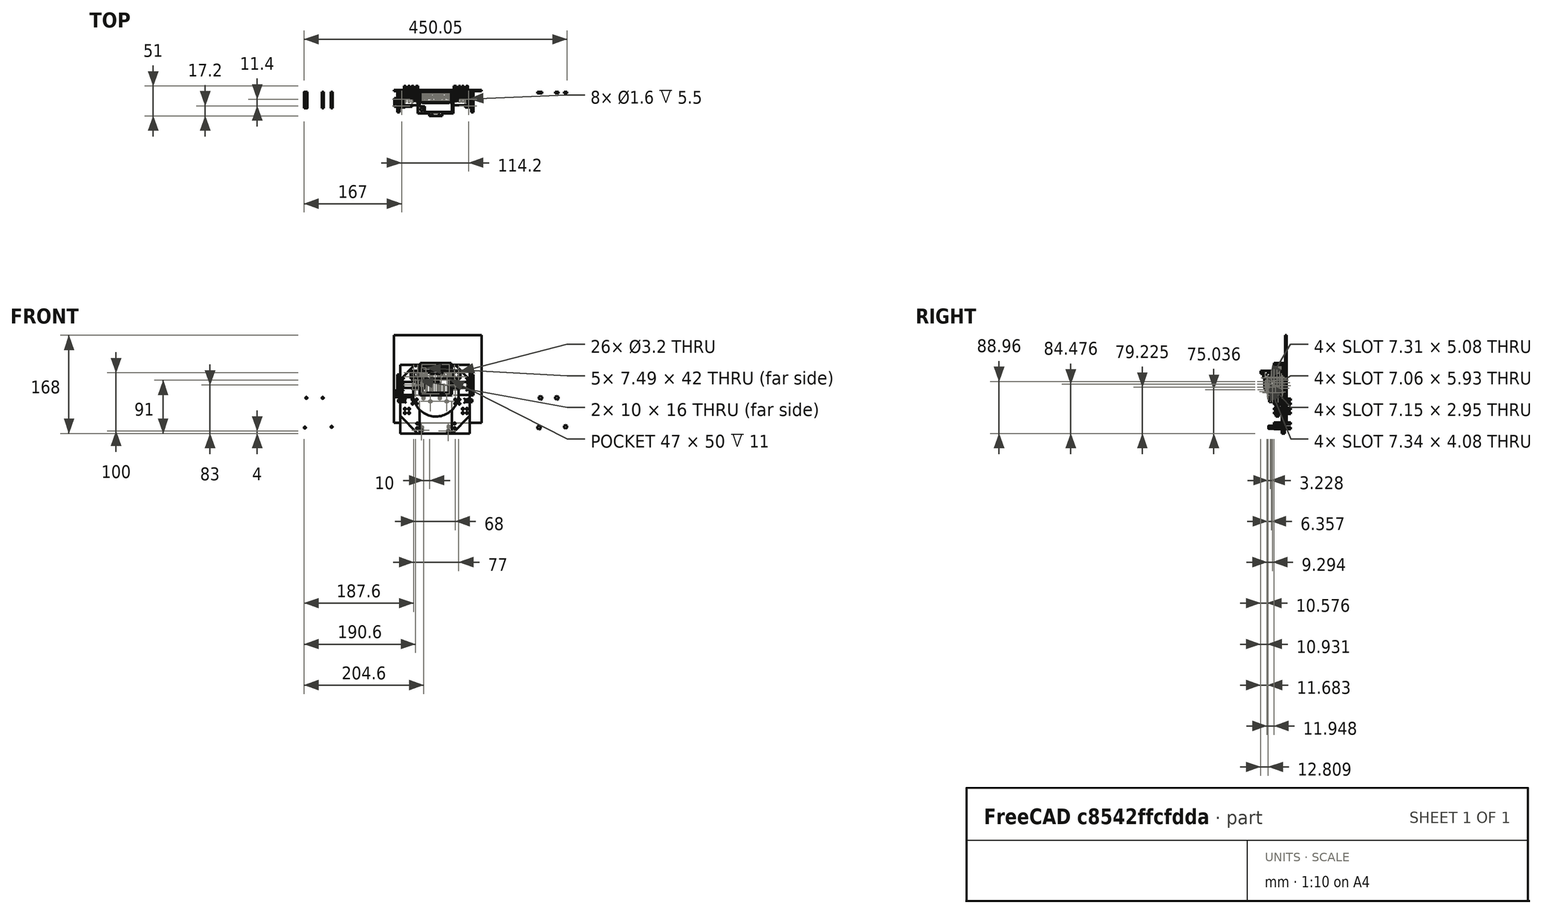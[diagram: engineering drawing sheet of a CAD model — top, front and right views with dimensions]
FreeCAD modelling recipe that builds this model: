
FCSTD DOCUMENT  (FreeCAD 0.16R6712 (Git))
Label: 5028.2 Frank the Robot
License: All rights reserved
LicenseURL: http://en.wikipedia.org/wiki/All_rights_reserved
objects: Part::Cylinder×87, Part::Cut×49, Part::Fuse×46, Part::Box×45, Part::MultiFuse×20, Part::Feature×17, Part::Fillet×10, Part::Mirroring×8, Part::Chamfer×7, Part::Cone×4, Part::Compound×3, Part::Torus×2, App::DocumentObjectGroup×1
note: 298 computed .brp shape members not serialized (recipe doc carries the construction recipe); baked Part::Feature solids carry a one-line shape summary decoded from their .brp

FEATURE [Part::Cylinder] Cylinder
  Angle = 360
  Height = 30
  Radius = 7
FEATURE [Part::Cylinder] Cylinder001
  Angle = 360
  Height = 19
  Placement = pos=(0,0,30) rot=(0,0,1;0rad)
  Radius = 7
FEATURE [Part::Cylinder] Cylinder002
  Angle = 360
  Height = 1.8
  Placement = pos=(0,0,49) rot=(0,0,1;0rad)
  Radius = 2.5
FEATURE [Part::Compound] Compound
  Links = -> [Cylinder,Cylinder002,Cylinder001]
FEATURE [Part::Cylinder] Cylinder003
  Angle = 360
  Height = 30
  Radius = 7
FEATURE [Part::Cylinder] Cylinder004
  Angle = 360
  Height = 19
  Placement = pos=(0,0,30) rot=(0,0,1;0rad)
  Radius = 7
FEATURE [Part::Cylinder] Cylinder005
  Angle = 360
  Height = 1.8
  Placement = pos=(0,0,49) rot=(0,0,1;0rad)
  Radius = 2.5
FEATURE [Part::Compound] Compound001
  Links = -> [Cylinder003,Cylinder005,Cylinder004]
  Placement = pos=(14.5,0,50) rot=(1,0,0;3.14159rad)
FEATURE [Part::Cylinder] Cylinder006
  Angle = 360
  Height = 30
  Radius = 7
FEATURE [Part::Cylinder] Cylinder007
  Angle = 360
  Height = 19
  Placement = pos=(0,0,30) rot=(0,0,1;0rad)
  Radius = 7
FEATURE [Part::Cylinder] Cylinder008
  Angle = 360
  Height = 1.8
  Placement = pos=(0,0,49) rot=(0,0,1;0rad)
  Radius = 2.5
FEATURE [Part::Compound] Compound002
  Links = -> [Cylinder006,Cylinder008,Cylinder007]
  Placement = pos=(29,0,0) rot=(0,0,1;0rad)
FEATURE [Part::Box] Box  label="Cube"
  Height = 50
  Length = 47
  Placement = pos=(-9,-8,0) rot=(0,0,1;0rad)
  Width = 12
FEATURE [Part::Box] Box001  label="Cube001"
  Height = 55
  Length = 53
  Placement = pos=(-12,-8,-2.5) rot=(0,0,1;0rad)
  Width = 11
FEATURE [Part::Cylinder] Cylinder009
  Angle = 360
  Height = 50
  Radius = 7
FEATURE [Part::Cylinder] Cylinder010
  Angle = 360
  Height = 50
  Placement = pos=(14.5,0,0) rot=(0,0,1;0rad)
  Radius = 7
FEATURE [Part::Cut] Cut
  Base = -> Box001
  Tool = -> Box
FEATURE [Part::Box] Box002  label="Cube002"
  Height = 55
  Length = 53
  Placement = pos=(-12,3,-2.5) rot=(0,0,1;0rad)
  Width = 7
FEATURE [Part::Fuse] Fusion
  Base = -> Cut
  Tool = -> Box002
FEATURE [Part::Cut] Cut001  label="No idea why this is here...."
  Base = -> Fusion
  Tool = -> Cylinder009
FEATURE [Part::Cylinder] Cylinder011
  Angle = 360
  Height = 50
  Placement = pos=(29,0,0) rot=(0,0,1;0rad)
  Radius = 7
FEATURE [Part::Box] Box003  label="Cube003"
  Height = 5
  Length = 2
  Placement = pos=(28,-9,-2) rot=(0,0,1;0rad)
  Width = 12
FEATURE [Part::Box] Box004  label="Cube004"
  Height = 5
  Length = 2
  Placement = pos=(18.5,-9,46) rot=(0,0,1;0rad)
  Width = 12
FEATURE [Part::Box] Box005  label="Cube005"
  Height = 5
  Length = 2
  Placement = pos=(-2,-9,46) rot=(0,0,1;0rad)
  Width = 12
FEATURE [Part::Box] Box006  label="Cube006"
  Height = 5
  Length = 3
  Placement = pos=(35,-9,-4) rot=(0,0,1;0rad)
  Width = 12
FEATURE [Part::Cut] Cut008
FEATURE [Part::Torus] Torus001
  Angle1 = -180
  Angle2 = 180
  Angle3 = 360
  Placement = pos=(0,0,2) rot=(0,0,1;0rad)
  Radius1 = 19
  Radius2 = 1.5
FEATURE [Part::Cut] Cut009  label="wheel2"
  Base = -> Cut008
  Placement = pos=(75,-7,15) rot=(0,1,0;1.5708rad)
  Tool = -> Torus001
FEATURE [Part::Torus] Torus
  Angle1 = -180
  Angle2 = 180
  Angle3 = 360
  Placement = pos=(0,0,2) rot=(0,0,1;0rad)
  Radius1 = 19
  Radius2 = 1.5
FEATURE [Part::Cut] Cut010
FEATURE [Part::Cut] Cut011  label="wheel1"
  Base = -> Cut010
  Placement = pos=(-51,-7,15) rot=(0,1,0;1.5708rad)
  Tool = -> Torus
FEATURE [Part::Fuse] Fusion003
FEATURE [Part::Cylinder] Cylinder012
  Angle = 360
  Height = 10
  Placement = pos=(5,-4.5,0) rot=(0,1,0;1.5708rad)
  Radius = 0.8
FEATURE [Part::Fuse] Fusion048  label="right-motor001"
  Base = -> Cylinder012
  Placement = pos=(-51,-7,15) rot=(0,0,1;0rad)
  Tool = -> Fusion003
FEATURE [Part::Fuse] Fusion049
FEATURE [Part::Cylinder] Cylinder013
  Angle = 360
  Height = 10
  Placement = pos=(5,-4.5,0) rot=(0,1,0;1.5708rad)
  Radius = 0.8
FEATURE [Part::Fuse] Fusion050  label="left-motor001"
  Base = -> Cylinder013
  Placement = pos=(79,-7,15) rot=(0,0,1;3.14159rad)
  Tool = -> Fusion049
FEATURE [Part::Box] Box007  label="Cube007"
  Height = 5
  Length = 2
  Placement = pos=(37.5,-9,46) rot=(0,0,1;0rad)
  Width = 12
FEATURE [Part::Box] Box008  label="Cube008"
  Height = 5
  Length = 2
  Placement = pos=(8,-9,-2) rot=(0,0,1;0rad)
  Width = 12
FEATURE [Part::Box] Box009  label="The Ground"
  Height = 150
  Length = 150
  Placement = pos=(-57,11,-50) rot=(0,0,1;0rad)
  Width = 2
FEATURE [Part::Box] Box010  label="Motor Mount Left"
  Height = 16
  Length = 4
  Placement = pos=(69,-13,7) rot=(0,0,1;0rad)
  Width = 20
FEATURE [Part::Box] Box011  label="Motor Mount Right"
  Height = 16
  Length = 4
  Placement = pos=(-46,-13,7) rot=(0,0,1;0rad)
  Width = 20
FEATURE [Part::Box] Box012  label="Motor Support Right"
  Height = 16
  Length = 10
  Placement = pos=(-25,-1,7) rot=(0,0,1;0rad)
  Width = 8
FEATURE [Part::Box] Box013  label="Motor Support Left"
  Height = 16
  Length = 10
  Placement = pos=(43,-1,7) rot=(0,0,1;0rad)
  Width = 8
FEATURE [Part::Cylinder] Cylinder014
  Angle = 360
  Height = 28
  Placement = pos=(40.7,0,-10.3) rot=(1,0,0;1.5708rad)
  Radius = 1.6
FEATURE [Part::Cylinder] Cylinder015
  Angle = 360
  Height = 28
  Placement = pos=(-2.4,0,-59.8) rot=(1,0,0;1.5708rad)
  Radius = 1.6
FEATURE [Part::Cylinder] Cylinder016
  Angle = 360
  Height = 28
  Placement = pos=(-5,0,-9) rot=(1,0,0;1.5708rad)
  Radius = 1.6
FEATURE [Part::Cylinder] Cylinder017
  Angle = 360
  Height = 28
  Placement = pos=(25.5,0,-59.8) rot=(1,0,0;1.5708rad)
  Radius = 1.6
FEATURE [Part::Fuse] Fusion051
  Base = -> Cylinder015
  Tool = -> Cylinder016
FEATURE [Part::Fuse] Fusion052
  Base = -> Cylinder014
  Tool = -> Cylinder017
FEATURE [Part::Fuse] Fusion053  label="Screw holes on Arduino Duo"
  Base = -> Fusion051
  Tool = -> Fusion052
FEATURE [Part::Mirroring] Part__Mirroring  label="XXXXXScrew holes on Arduino Duo (Mirror #1)"
  Base = (0,0,0)
  Normal = (0,0,1)
  Placement = pos=(-204,10,-67) rot=(0,0,1;0rad)
  Source = -> Fusion053
FEATURE [Part::Box] Box014  label="Not used Cube"
  Height = 51
  Length = 119
  Placement = pos=(-46,7,-2) rot=(0,0,1;0rad)
  Width = 3
FEATURE [Part::Box] Box015  label="Cube014 Arduino Support cube"
  Height = 67
  Length = 55
  Placement = pos=(-13,5,-68) rot=(0,0,1;0rad)
  Width = 5
FEATURE [Part::Cylinder] Cylinder018
  Angle = 360
  Height = 5
  Placement = pos=(15,0,0) rot=(1,0,0;1.5708rad)
  Radius = 39
FEATURE [Part::Cut] Cut014  label="M3 Nut"
  Base = -> Cut001
  Placement = pos=(-6.4,10,-7.2) rot=(1,0,0;1.5708rad)
  Tool = -> Cylinder001
FEATURE [Part::Cut] Cut015  label="M3 Nut001"
  Base = -> Cut001
  Placement = pos=(21.5,10,-7.2) rot=(1,0,0;1.5708rad)
  Tool = -> Cylinder001
FEATURE [Part::Cut] Cut016  label="M3 Nut002"
  Base = -> Cut001
  Placement = pos=(36.7,10,-56.7) rot=(1,0,0;1.5708rad)
  Tool = -> Cylinder001
FEATURE [Part::Cut] Cut017  label="M3 Nut003"
  Base = -> Cut001
  Placement = pos=(-9,10,-58) rot=(1,0,0;1.5708rad)
  Tool = -> Cylinder001
FEATURE [Part::Cut] Cut018
  Base = -> Cut
  Placement = pos=(-9,10,-58) rot=(1,0,0;1.5708rad)
  Tool = -> Box006
FEATURE [Part::Cut] Cut019
  Base = -> Cut
  Placement = pos=(36.7,10,-56.7) rot=(1,0,0;1.5708rad)
  Tool = -> Box006
FEATURE [Part::Cut] Cut020
  Base = -> Cut
  Placement = pos=(-6.4,10,-7.2) rot=(1,0,0;1.5708rad)
  Tool = -> Box006
FEATURE [Part::Cut] Cut021
  Base = -> Cut
  Placement = pos=(21.5,10,-7.2) rot=(1,0,0;1.5708rad)
  Tool = -> Box006
FEATURE [Part::MultiFuse] Fusion054  label="XXXXXHex Holes"
  Placement = pos=(200,0,0) rot=(0,0,1;0rad)
  Shapes = -> [Cut018,Cut021,Cut019,Cut020]
FEATURE [Part::Box] Box016  label="Cube015"
  Height = 117
  Length = 33
  Placement = pos=(-46,7,-68) rot=(0,0,1;0rad)
  Width = 3
FEATURE [Part::Box] Box017  label="Cube016"
  Height = 117
  Length = 31
  Placement = pos=(42,7,-68) rot=(0,0,1;0rad)
  Width = 3
FEATURE [Part::Cylinder] Cylinder019
  Angle = 360
  Height = 28
  Placement = pos=(48,20,-10) rot=(1,0,0;1.5708rad)
  Radius = 1.6
FEATURE [Part::Cylinder] Cylinder020
  Angle = 360
  Height = 28
  Placement = pos=(47,20,-51) rot=(1,0,0;1.5708rad)
  Radius = 1.6
FEATURE [Part::Cylinder] Cylinder021
  Angle = 360
  Height = 28
  Placement = pos=(48,20,-17) rot=(1,0,0;1.5708rad)
  Radius = 1.6
FEATURE [Part::Cylinder] Cylinder022
  Angle = 360
  Height = 28
  Placement = pos=(47,20,-59) rot=(1,0,0;1.5708rad)
  Radius = 1.6
FEATURE [Part::Cylinder] Cylinder023
  Angle = 360
  Height = 28
  Placement = pos=(55,20,-17) rot=(1,0,0;1.5708rad)
  Radius = 1.6
FEATURE [Part::Cylinder] Cylinder024
  Angle = 360
  Height = 28
  Placement = pos=(55,20,-10) rot=(1,0,0;1.5708rad)
  Radius = 1.6
FEATURE [Part::MultiFuse] Fusion055
  Shapes = -> [Cylinder021,Cylinder023,Cylinder024,Cylinder019]
FEATURE [Part::MultiFuse] Fusion056
  Placement = pos=(13,0,-16) rot=(0,0,1;0rad)
  Shapes = -> [Cylinder021,Cylinder023,Cylinder024,Cylinder019]
FEATURE [Part::MultiFuse] Fusion057  label="Mount holes top left"
  Placement = pos=(-1,0,46) rot=(0,0,1;0rad)
  Shapes = -> [Cylinder021,Cylinder023,Cylinder024,Cylinder019]
FEATURE [Part::MultiFuse] Fusion058  label="Mount holes top right"
  Placement = pos=(-71,0,46) rot=(0,0,1;0rad)
  Shapes = -> [Cylinder021,Cylinder023,Cylinder024,Cylinder019]
FEATURE [Part::MultiFuse] Fusion059
  Shapes = -> [Cylinder022,Cylinder020,Fusion055,Fusion056]
FEATURE [Part::Mirroring] Part__Mirroring001  label="Mount holes bottom right"
  Base = (0,0,0)
  Normal = (1,0,0)
  Placement = pos=(30,0,0) rot=(0,0,1;0rad)
  Source = -> Fusion059
FEATURE [Part::Cylinder] Cylinder025
  Angle = 360
  Height = 28
  Placement = pos=(48,20,-10) rot=(1,0,0;1.5708rad)
  Radius = 1.6
FEATURE [Part::Cylinder] Cylinder026
  Angle = 360
  Height = 28
  Placement = pos=(47,20,-51) rot=(1,0,0;1.5708rad)
  Radius = 1.6
FEATURE [Part::Cylinder] Cylinder027
  Angle = 360
  Height = 28
  Placement = pos=(48,20,-17) rot=(1,0,0;1.5708rad)
  Radius = 1.6
FEATURE [Part::Cylinder] Cylinder028
  Angle = 360
  Height = 28
  Placement = pos=(47,20,-59) rot=(1,0,0;1.5708rad)
  Radius = 1.6
FEATURE [Part::Cylinder] Cylinder029
  Angle = 360
  Height = 28
  Placement = pos=(55,20,-17) rot=(1,0,0;1.5708rad)
  Radius = 1.6
FEATURE [Part::Cylinder] Cylinder030
  Angle = 360
  Height = 28
  Placement = pos=(55,20,-10) rot=(1,0,0;1.5708rad)
  Radius = 1.6
FEATURE [Part::MultiFuse] Fusion060
  Shapes = -> [Cylinder027,Cylinder029,Cylinder030,Cylinder025]
FEATURE [Part::MultiFuse] Fusion061
  Placement = pos=(13,0,-16) rot=(0,0,1;0rad)
  Shapes = -> [Cylinder027,Cylinder029,Cylinder030,Cylinder025]
FEATURE [Part::MultiFuse] Fusion062  label="Mount holes bottom left"
  Shapes = -> [Cylinder028,Cylinder026,Fusion060,Fusion061]
FEATURE [Part::Cylinder] Cylinder031  label="Cylinder083"
  Angle = 360
  Height = 10
  Placement = pos=(0,18,29) rot=(0,0,1;0rad)
  Radius = 2.25
FEATURE [Part::Cylinder] Cylinder032  label="Cylinder084"
  Angle = 360
  Height = 10
  Placement = pos=(4.5,18,32) rot=(0,0,1;0rad)
  Radius = 1
FEATURE [Part::Cylinder] Cylinder033  label="Cylinder085"
  Angle = 360
  Height = 10
  Placement = pos=(-4.5,18,32) rot=(0,0,1;0rad)
  Radius = 1
FEATURE [Part::Fuse] Fusion009  label="Mounting Screw Holes"
  Base = -> Cylinder032
  Tool = -> Cylinder033
FEATURE [Part::Fuse] Fusion071  label="Motor Holes Left"
  Base = -> Cylinder031
  Placement = pos=(37,-7,-3) rot=(0.57735,0.57735,0.57735;2.0944rad)
  Tool = -> Fusion009
FEATURE [Part::Cylinder] Cylinder034  label="Cylinder086"
  Angle = 360
  Height = 10
  Placement = pos=(0,18,29) rot=(0,0,1;0rad)
  Radius = 2.25
FEATURE [Part::Cylinder] Cylinder035  label="Cylinder087"
  Angle = 360
  Height = 10
  Placement = pos=(4.5,18,32) rot=(0,0,1;0rad)
  Radius = 1
FEATURE [Part::Cylinder] Cylinder036  label="Cylinder088"
  Angle = 360
  Height = 10
  Placement = pos=(-4.5,18,32) rot=(0,0,1;0rad)
  Radius = 1
FEATURE [Part::Fuse] Fusion072  label="Mounting Screw Holes001"
  Base = -> Cylinder035
  Tool = -> Cylinder036
FEATURE [Part::Fuse] Fusion073  label="Motor Holes Right"
  Base = -> Cylinder034
  Placement = pos=(-79,-7,-3) rot=(0.57735,0.57735,0.57735;2.0944rad)
  Tool = -> Fusion072
FEATURE [Part::Cylinder] Cylinder037  label="Cylinder089"
  Angle = 360
  Height = 28
  Placement = pos=(40.7,0,-10.3) rot=(1,0,0;1.5708rad)
  Radius = 1.6
FEATURE [Part::Cylinder] Cylinder038  label="Cylinder090"
  Angle = 360
  Height = 28
  Placement = pos=(-2.4,0,-59.8) rot=(1,0,0;1.5708rad)
  Radius = 1.6
FEATURE [Part::Cylinder] Cylinder039  label="Cylinder091"
  Angle = 360
  Height = 28
  Placement = pos=(-5,0,-9) rot=(1,0,0;1.5708rad)
  Radius = 1.6
FEATURE [Part::Cylinder] Cylinder040  label="Cylinder092"
  Angle = 360
  Height = 28
  Placement = pos=(25.5,0,-59.8) rot=(1,0,0;1.5708rad)
  Radius = 1.6
FEATURE [Part::Fuse] Fusion074
  Base = -> Cylinder038
  Tool = -> Cylinder039
FEATURE [Part::Fuse] Fusion075
  Base = -> Cylinder037
  Tool = -> Cylinder040
FEATURE [Part::Fuse] Fusion076  label="Screw holes on Arduino Duo001"
  Base = -> Fusion074
  Tool = -> Fusion075
FEATURE [Part::Mirroring] Part__Mirroring002  label="Screw holes on Arduino Duo (Mirror #1)001"
  Base = (0,0,0)
  Normal = (0,0,1)
  Placement = pos=(-4,10,-67) rot=(0,0,1;0rad)
  Source = -> Fusion076
FEATURE [Part::Mirroring] Part__Mirroring003  label="Screw holes on Arduino Duo (Mirror #1)001 (Mirror #4)"
  Base = (0,0,0)
  Normal = (1,0,0)
  Placement = pos=(27,0,-6) rot=(0,0,1;0rad)
  Source = -> Part__Mirroring002
FEATURE [Part::Box] Box018  label="Cube017"
  Height = 50
  Length = 47
  Placement = pos=(-9,-8,0) rot=(0,0,1;0rad)
  Width = 12
FEATURE [Part::Box] Box019  label="Cube018"
  Height = 55
  Length = 53
  Placement = pos=(-12,-8,-2.5) rot=(0,0,1;0rad)
  Width = 11
FEATURE [Part::Cut] Cut031
  Base = -> Box019
  Tool = -> Box018
FEATURE [Part::Box] Box020  label="Cube019"
  Height = 5
  Length = 3
  Placement = pos=(35,-9,-4) rot=(0,0,1;0rad)
  Width = 12
FEATURE [Part::Cut] Cut032
  Base = -> Cut031
  Placement = pos=(-9,10,-58) rot=(1,0,0;1.5708rad)
  Tool = -> Box020
FEATURE [Part::Cut] Cut033
  Base = -> Cut031
  Placement = pos=(36.7,10,-56.7) rot=(1,0,0;1.5708rad)
  Tool = -> Box020
FEATURE [Part::Cut] Cut034
  Base = -> Cut031
  Placement = pos=(-6.4,10,-7.2) rot=(1,0,0;1.5708rad)
  Tool = -> Box020
FEATURE [Part::Cut] Cut035
  Base = -> Cut031
  Placement = pos=(21.5,10,-7.2) rot=(1,0,0;1.5708rad)
  Tool = -> Box020
FEATURE [Part::MultiFuse] Fusion077
  Shapes = -> [Cut032,Cut035,Cut033,Cut034]
FEATURE [Part::Mirroring] Part__Mirroring004  label="Hex Holes"
  Base = (0,0,0)
  Normal = (1,0,0)
  Placement = pos=(27,0,-6) rot=(0,0,1;0rad)
  Source = -> Fusion077
FEATURE [Part::Box] Box021  label="Cube020"
  Height = 13
  Length = 61
  Placement = pos=(-16,-27,26) rot=(0,0,1;0rad)
  Width = 34
FEATURE [Part::Box] Box022  label="Cube021"
  Height = 13
  Length = 12
  Placement = pos=(45,4,26) rot=(0,0,1;0rad)
  Width = 3
FEATURE [Part::Box] Box023  label="Cube022"
  Height = 13
  Length = 12
  Placement = pos=(-28,4,26) rot=(0,0,1;0rad)
  Width = 3
FEATURE [Part::Box] Box024  label="Cube023"
  Height = 13
  Length = 55
  Placement = pos=(-13,-24,26) rot=(0,0,1;0rad)
  Width = 31
FEATURE [Part::Cylinder] Cylinder041  label="Cylinder093"
  Angle = 360
  Height = 28
  Placement = pos=(54,20,29) rot=(1,0,0;1.5708rad)
  Radius = 1.6
FEATURE [Part::Cylinder] Cylinder042  label="Cylinder094"
  Angle = 360
  Height = 28
  Placement = pos=(54,20,36) rot=(1,0,0;1.5708rad)
  Radius = 1.6
FEATURE [Part::Cylinder] Cylinder043  label="Cylinder095"
  Angle = 360
  Height = 28
  Placement = pos=(-23,20,29) rot=(1,0,0;1.5708rad)
  Radius = 1.6
FEATURE [Part::Cylinder] Cylinder044  label="Cylinder096"
  Angle = 360
  Height = 28
  Placement = pos=(-23,20,36) rot=(1,0,0;1.5708rad)
  Radius = 1.6
FEATURE [Part::Cylinder] Cylinder045  label="Cylinder097"
  Angle = 360
  Height = 10
  Placement = pos=(36,-17.25,32.5) rot=(0,1,0;1.5708rad)
  Radius = 3.25
FEATURE [Part::Cut] Cut037
  Base = -> Box021
  Tool = -> Box024
FEATURE [Part::Cut] Cut038
  Base = -> Cut037
  Tool = -> Cylinder045
FEATURE [Part::Box] Box025  label="Cube024"
  Height = 5
  Length = 22
  Placement = pos=(3.5,-31,34) rot=(0,0,1;0rad)
  Width = 4
FEATURE [Part::Cylinder] Cylinder046  label="Cylinder098"
  Angle = 360
  Height = 10
  Placement = pos=(20.65,-29,30) rot=(0,0,1;0rad)
  Radius = 0.85
FEATURE [Part::Cylinder] Cylinder047  label="Cylinder099"
  Angle = 360
  Height = 10
  Placement = pos=(8.35,-29,40) rot=(1,0,0;3.14159rad)
  Radius = 0.85
FEATURE [Part::Fuse] Fusion078
  Base = -> Cylinder046
  Tool = -> Cylinder047
FEATURE [Part::Cut] Cut039
  Base = -> Box025
  Tool = -> Fusion078
FEATURE [Part::Fuse] Fusion079
  Base = -> Cut038
  Tool = -> Cut039
FEATURE [Part::Fuse] Fusion080
  Base = -> Cylinder043
  Tool = -> Cylinder044
FEATURE [Part::Fuse] Fusion081
  Base = -> Cylinder041
  Tool = -> Cylinder042
FEATURE [Part::Fuse] Fusion082
  Base = -> Box023
  Tool = -> Fusion079
FEATURE [Part::Fuse] Fusion083
  Base = -> Box022
  Tool = -> Fusion082
FEATURE [Part::Cut] Cut040
  Base = -> Fusion083
  Tool = -> Fusion081
FEATURE [Part::Cut] Cut041  label="Switch Bracket"
  Base = -> Cut040
  Tool = -> Fusion080
FEATURE [Part::Cylinder] Cylinder048  label="Cylinder100"
  Angle = 360
  Height = 28
  Placement = pos=(-23,20,29) rot=(1,0,0;1.5708rad)
  Radius = 1.6
FEATURE [Part::Cylinder] Cylinder049  label="Cylinder101"
  Angle = 360
  Height = 28
  Placement = pos=(-23,20,36) rot=(1,0,0;1.5708rad)
  Radius = 1.6
FEATURE [Part::Fuse] Fusion084
  Base = -> Cylinder048
  Placement = pos=(1,0,0) rot=(0,0,1;0rad)
  Tool = -> Cylinder049
FEATURE [Part::Cylinder] Cylinder050  label="Cylinder102"
  Angle = 360
  Height = 28
  Placement = pos=(-23,20,29) rot=(1,0,0;1.5708rad)
  Radius = 1.6
FEATURE [Part::Cylinder] Cylinder051  label="Cylinder103"
  Angle = 360
  Height = 28
  Placement = pos=(-23,20,36) rot=(1,0,0;1.5708rad)
  Radius = 1.6
FEATURE [Part::Fuse] Fusion085
  Base = -> Cylinder050
  Placement = pos=(-1,0,0) rot=(0,0,1;0rad)
  Tool = -> Cylinder051
FEATURE [Part::Cut] Cut042
  Base = -> Cut041
  Tool = -> Fusion084
FEATURE [Part::Cut] Cut043  label="Switch Bracket001"
  Base = -> Cut042
  Tool = -> Fusion085
FEATURE [Part::Cylinder] Cylinder052  label="Cylinder104"
  Angle = 360
  Height = 42
  Radius = 4.8
FEATURE [Part::Cylinder] Cylinder053  label="Cylinder105"
  Angle = 360
  Height = 1.6
  Placement = pos=(0,0,42) rot=(0,0,1;0rad)
  Radius = 1.65
FEATURE [Part::Fuse] Fusion086
  Base = -> Cylinder052
  Placement = pos=(2,0,0) rot=(0,0,1;0rad)
  Tool = -> Cylinder053
FEATURE [Part::Cylinder] Cylinder054  label="Cylinder106"
  Angle = 360
  Height = 42
  Radius = 4.8
FEATURE [Part::Cylinder] Cylinder055  label="Cylinder107"
  Angle = 360
  Height = 1.6
  Placement = pos=(0,0,42) rot=(0,0,1;0rad)
  Radius = 1.65
FEATURE [Part::Fuse] Fusion087
  Base = -> Cylinder054
  Placement = pos=(12,0,0) rot=(0,0,1;0rad)
  Tool = -> Cylinder055
FEATURE [Part::Cylinder] Cylinder056  label="Cylinder108"
  Angle = 360
  Height = 42
  Radius = 4.8
FEATURE [Part::Cylinder] Cylinder057  label="Cylinder109"
  Angle = 360
  Height = 1.6
  Placement = pos=(0,0,42) rot=(0,0,1;0rad)
  Radius = 1.65
FEATURE [Part::Fuse] Fusion088
  Base = -> Cylinder056
  Placement = pos=(22,0,0) rot=(0,0,1;0rad)
  Tool = -> Cylinder057
FEATURE [Part::Cylinder] Cylinder058  label="Cylinder110"
  Angle = 360
  Height = 42
  Radius = 4.8
FEATURE [Part::Cylinder] Cylinder059  label="Cylinder111"
  Angle = 360
  Height = 1.6
  Placement = pos=(0,0,42) rot=(0,0,1;0rad)
  Radius = 1.65
FEATURE [Part::Fuse] Fusion089
  Base = -> Cylinder058
  Placement = pos=(32,0,0) rot=(0,0,1;0rad)
  Tool = -> Cylinder059
FEATURE [Part::Cylinder] Cylinder060  label="Cylinder112"
  Angle = 360
  Height = 42
  Radius = 4.8
FEATURE [Part::Cylinder] Cylinder061  label="Cylinder113"
  Angle = 360
  Height = 1.6
  Placement = pos=(0,0,42) rot=(0,0,1;0rad)
  Radius = 1.65
FEATURE [Part::Fuse] Fusion093
  Base = -> Cylinder060
  Placement = pos=(-8,0,0) rot=(0,0,1;0rad)
  Tool = -> Cylinder061
FEATURE [Part::MultiFuse] Fusion094  label="AAA Batts"
  Placement = pos=(2.5,0,2) rot=(0,0,1;0rad)
  Shapes = -> [Fusion093,Fusion086,Fusion087,Fusion088,Fusion089]
FEATURE [Part::Cylinder] Cylinder062  label="Cylinder114"
  Angle = 360
  Height = 10
  Radius = 17
FEATURE [Part::Cylinder] Cylinder063  label="Cylinder115"
  Angle = 360
  Height = 16
  Placement = pos=(0,0,-4) rot=(0,0,1;0rad)
  Radius = 10
FEATURE [Part::Cut] Cut044
  Base = -> Cylinder062
  Tool = -> Cylinder063
FEATURE [Part::Box] Box026  label="Cube025"
  Height = 20
  Length = 18
  Placement = pos=(0,0,-5) rot=(0,0,1;0rad)
  Width = 20
FEATURE [Part::Box] Box027  label="Cube026"
  Height = 20
  Length = 10
  Placement = pos=(0,0,-5) rot=(0,0,1;0.174533rad)
  Width = 20
FEATURE [Part::Cut] Cut045
  Base = -> Box027
  Tool = -> Box026
FEATURE [Part::Feature] Cut045001
  Placement = pos=(0,0,0) rot=(0,0,1;0.349066rad)
  shape: bbox 10 x 22.32 x 20 mm, 7 faces (baked)
FEATURE [Part::Feature] Cut045002
  Placement = pos=(0,0,0) rot=(0,0,1;0.698132rad)
  shape: bbox 15.32 x 20.52 x 20 mm, 7 faces (baked)
FEATURE [Part::Feature] Cut045003
  Placement = pos=(0,0,0) rot=(0,0,1;1.0472rad)
  shape: bbox 18.79 x 16.24 x 20 mm, 7 faces (baked)
FEATURE [Part::Feature] Cut045004
  Placement = pos=(0,0,0) rot=(0,0,1;1.39626rad)
  shape: bbox 20 x 10 x 20 mm, 7 faces (baked)
FEATURE [Part::Feature] Cut045005
  Placement = pos=(0,0,0) rot=(0,0,1;1.74533rad)
  shape: bbox 22.21 x 9.894 x 20 mm, 7 faces (baked)
FEATURE [Part::Feature] Cut045006
  Placement = pos=(0,0,0) rot=(0,0,1;2.0944rad)
  shape: bbox 21.75 x 12.86 x 20 mm, 7 faces (baked)
FEATURE [Part::Feature] Cut045007
  Placement = pos=(0,0,0) rot=(0,0,1;2.44346rad)
  shape: bbox 18.66 x 17.32 x 20 mm, 7 faces (baked)
FEATURE [Part::Feature] Cut045008
  Placement = pos=(0,0,0) rot=(0,0,1;2.79253rad)
  shape: bbox 13.32 x 19.7 x 20 mm, 7 faces (baked)
FEATURE [Part::Feature] Cut045009
  Placement = pos=(0,0,0) rot=(0,0,1;3.14159rad)
  shape: bbox 10.1 x 21.43 x 20 mm, 7 faces (baked)
FEATURE [Part::Feature] Cut045010
  Placement = pos=(0,0,0) rot=(0,0,1;3.49066rad)
  shape: bbox 10 x 22.32 x 20 mm, 7 faces (baked)
FEATURE [Part::Feature] Cut045011
  Placement = pos=(0,0,0) rot=(0,0,1;3.83972rad)
  shape: bbox 15.32 x 20.52 x 20 mm, 7 faces (baked)
FEATURE [Part::Feature] Cut045012
  Placement = pos=(0,0,0) rot=(0,0,1;4.18879rad)
  shape: bbox 18.79 x 16.24 x 20 mm, 7 faces (baked)
FEATURE [Part::Feature] Cut045013
  Placement = pos=(0,0,0) rot=(0,0,-1;1.74533rad)
  shape: bbox 20 x 10 x 20 mm, 7 faces (baked)
FEATURE [Part::Feature] Cut045014
  Placement = pos=(0,0,0) rot=(0,0,-1;1.39626rad)
  shape: bbox 22.21 x 9.894 x 20 mm, 7 faces (baked)
FEATURE [Part::Feature] Cut045015
  Placement = pos=(0,0,0) rot=(0,0,-1;1.0472rad)
  shape: bbox 21.75 x 12.86 x 20 mm, 7 faces (baked)
FEATURE [Part::Feature] Cut045016
  Placement = pos=(0,0,0) rot=(0,0,-1;0.698132rad)
  shape: bbox 18.66 x 17.32 x 20 mm, 7 faces (baked)
FEATURE [Part::Feature] Cut045017
  Placement = pos=(0,0,0) rot=(0,0,-1;0.349066rad)
  shape: bbox 13.32 x 19.7 x 20 mm, 7 faces (baked)
FEATURE [Part::MultiFuse] Fusion095
  Shapes = -> [Cut045001,Cut045008,Cut045010,Cut045009,Cut045005,Cut045003,Cut045006,Cut045002,Cut045004,Cut045007,Cut045016,Cut045017,Cut045011,Cut045012,Cut045013,Cut045014,Cut045015,Cut045]
FEATURE [Part::Cut] Cut045018
  Base = -> Cut044
  Placement = pos=(72,-7,15) rot=(0,1,0;1.5708rad)
  Tool = -> Fusion095
FEATURE [Part::Cut] Cut045019  label="Wheel with Spokes AB"
  Base = -> Cut009
  Tool = -> Cut045018
FEATURE [Part::Box] Box028  label="Cube027"
  Height = 5
  Length = 2
  Placement = pos=(37.5,-9,-2) rot=(0,0,1;0rad)
  Width = 12
FEATURE [Part::Box] Box029  label="Cube028"
  Height = 50
  Length = 47
  Placement = pos=(-9,-8,0) rot=(0,0,1;0rad)
  Width = 12
FEATURE [Part::Box] Box030  label="Cube029"
  Height = 55
  Length = 53
  Placement = pos=(-12,-8,-2.5) rot=(0,0,1;0rad)
  Width = 11
FEATURE [Part::Cylinder] Cylinder064  label="Cylinder116"
  Angle = 360
  Height = 50
  Radius = 7
FEATURE [Part::Cut] Cut045020
  Base = -> Box030
  Tool = -> Box029
FEATURE [Part::Box] Box031  label="Cube030"
  Height = 55
  Length = 53
  Placement = pos=(-12,3,-2.5) rot=(0,0,1;0rad)
  Width = 7
FEATURE [Part::Fuse] Fusion096
  Base = -> Cut045020
  Tool = -> Box031
FEATURE [App::DocumentObjectGroup] Group  label="Older version parts"
  Group = -> [Compound,Compound001,Compound002,Cylinder064,Cylinder010,Cylinder011,Fusion096,Part__Mirroring,Fusion054,Part__Mirroring001,Fusion062]
FEATURE [Part::Box] Box032  label="Battery Base"
  Height = 50
  Length = 55
  Placement = pos=(-13,3,-1) rot=(0,0,1;0rad)
  Width = 7
FEATURE [Part::Box] Box033  label="Cube031"
  Height = 30
  Length = 10
  Placement = pos=(-14,-25,9) rot=(0,0,1;0rad)
  Width = 10
FEATURE [Part::Cylinder] Cylinder065  label="Cylinder117"
  Angle = 360
  Height = 42
  Radius = 4.8
FEATURE [Part::Cylinder] Cylinder066  label="Cylinder118"
  Angle = 360
  Height = 1.6
  Placement = pos=(0,0,42) rot=(0,0,1;0rad)
  Radius = 1.65
FEATURE [Part::Fuse] Fusion097
  Base = -> Cylinder065
  Placement = pos=(2,0,0) rot=(0,0,1;0rad)
  Tool = -> Cylinder066
FEATURE [Part::Cylinder] Cylinder067  label="Cylinder119"
  Angle = 360
  Height = 42
  Radius = 4.8
FEATURE [Part::Cylinder] Cylinder068  label="Cylinder120"
  Angle = 360
  Height = 1.6
  Placement = pos=(0,0,42) rot=(0,0,1;0rad)
  Radius = 1.65
FEATURE [Part::Fuse] Fusion098
  Base = -> Cylinder067
  Placement = pos=(12,0,0) rot=(0,0,1;0rad)
  Tool = -> Cylinder068
FEATURE [Part::Cylinder] Cylinder069  label="Cylinder121"
  Angle = 360
  Height = 42
  Radius = 4.8
FEATURE [Part::Cylinder] Cylinder070  label="Cylinder122"
  Angle = 360
  Height = 1.6
  Placement = pos=(0,0,42) rot=(0,0,1;0rad)
  Radius = 1.65
FEATURE [Part::Fuse] Fusion099
  Base = -> Cylinder069
  Placement = pos=(22,0,0) rot=(0,0,1;0rad)
  Tool = -> Cylinder070
FEATURE [Part::Cylinder] Cylinder071  label="Cylinder123"
  Angle = 360
  Height = 42
  Radius = 4.8
FEATURE [Part::Cylinder] Cylinder072  label="Cylinder124"
  Angle = 360
  Height = 1.6
  Placement = pos=(0,0,42) rot=(0,0,1;0rad)
  Radius = 1.65
FEATURE [Part::Fuse] Fusion100
  Base = -> Cylinder071
  Placement = pos=(32,0,0) rot=(0,0,1;0rad)
  Tool = -> Cylinder072
FEATURE [Part::Cylinder] Cylinder073  label="Cylinder125"
  Angle = 360
  Height = 42
  Radius = 4.8
FEATURE [Part::Cylinder] Cylinder074  label="Cylinder126"
  Angle = 360
  Height = 1.6
  Placement = pos=(0,0,42) rot=(0,0,1;0rad)
  Radius = 1.65
FEATURE [Part::Fuse] Fusion101
  Base = -> Cylinder073
  Placement = pos=(-8,0,0) rot=(0,0,1;0rad)
  Tool = -> Cylinder074
FEATURE [Part::MultiFuse] Fusion102  label="AAA Batts001"
  Placement = pos=(2,0,2) rot=(0,0,1;0rad)
  Shapes = -> [Fusion101,Fusion097,Fusion098,Fusion099,Fusion100]
FEATURE [Part::Cylinder] Cylinder075  label="Cylinder127"
  Angle = 360
  Height = 10
  Placement = pos=(-9,-20,4) rot=(0,0,1;0rad)
  Radius = 2.75
FEATURE [Part::Cylinder] Cylinder076  label="Cylinder128"
  Angle = 360
  Height = 27
  Placement = pos=(-9,-20,14) rot=(0,0,1;0rad)
  Radius = 2.5
FEATURE [Part::Fuse] Fusion103  label="phototransistor hole"
  Base = -> Cylinder075
  Tool = -> Cylinder076
FEATURE [Part::Cut] Cut045021
  Base = -> Box033
  Tool = -> Fusion103
FEATURE [Part::Fuse] Fusion104  label="Switch Mount with phototransistor hole"
  Base = -> Cut043
  Tool = -> Cut045021
FEATURE [Part::Cut] Cut045022
  Base = -> Box032
  Tool = -> Fusion102
FEATURE [Part::Box] Box034  label="Cube032"
  Height = 2.5
  Length = 55
  Placement = pos=(-13,-9,-1) rot=(0,0,1;0rad)
  Width = 12
FEATURE [Part::Box] Box035  label="Cube033"
  Height = 2.5
  Length = 55
  Placement = pos=(-13,-9,46.5) rot=(0,0,1;0rad)
  Width = 12
FEATURE [Part::Box] Box036  label="Cube034"
  Height = 50
  Length = 2.5
  Placement = pos=(-13,-9,-1) rot=(0,0,1;0rad)
  Width = 12
FEATURE [Part::Box] Box037  label="Cube035"
  Height = 50
  Length = 2.5
  Placement = pos=(39.5,-9,-1) rot=(0,0,1;0rad)
  Width = 12
FEATURE [Part::MultiFuse] Fusion105
  Shapes = -> [Box034,Box036,Box037,Box035]
FEATURE [Part::Box] Box038  label="Cube036"
  Height = 5
  Length = 2
  Placement = pos=(-10.5,-9,46) rot=(0,0,1;0rad)
  Width = 12
FEATURE [Part::Box] Box039  label="Cube037"
  Height = 5
  Length = 2
  Placement = pos=(-10.5,-9,-2) rot=(0,0,1;0rad)
  Width = 12
FEATURE [Part::MultiFuse] Fusion106
  Shapes = -> [Box039,Box038,Box028,Box007]
FEATURE [Part::MultiFuse] Fusion107
  Shapes = -> [Box003,Box004,Box005,Box008]
FEATURE [Part::Cut] Cut045023
  Base = -> Fusion105
  Tool = -> Fusion106
FEATURE [Part::Cut] Cut045024
  Base = -> Cut045023
  Tool = -> Fusion107
FEATURE [Part::Box] Box040  label="Cube038"
  Height = 1.6
  Length = 30
  Placement = pos=(-56,-15.5,-6) rot=(0,0,1;0rad)
  Width = 15
FEATURE [Part::Box] Box041  label="Cube039"
  Height = 10
  Length = 14
  Placement = pos=(-56,-10.5,-4.5) rot=(0,0,1;0rad)
  Width = 6
FEATURE [Part::Box] Box042  label="Cube040"
  Height = 10
  Length = 5.3
  Placement = pos=(-51.7,-11.5,-4.5) rot=(0,0,1;0rad)
  Width = 8
FEATURE [Part::Cut] Cut045025
  Base = -> Box041
  Tool = -> Box042
FEATURE [Part::Fuse] Fusion108  label="Spoke Sensor PCB"
  Base = -> Box040
  Tool = -> Cut045025
FEATURE [Part::Cylinder] Cylinder077  label="Cylinder129"
  Angle = 360
  Height = 14.5
  Placement = pos=(-43.6,-2.4,-9) rot=(0,0,1;0rad)
  Radius = 0.8
FEATURE [Part::Cylinder] Cylinder078  label="Cylinder130"
  Angle = 360
  Height = 14.5
  Placement = pos=(-43.6,-13.8,-9) rot=(0,0,1;0rad)
  Radius = 0.8
FEATURE [Part::Fuse] Fusion109
  Base = -> Cylinder077
  Tool = -> Cylinder078
FEATURE [Part::Cut] Cut045026  label="Spoke Sensor PCB001"
  Base = -> Fusion108
  Tool = -> Fusion109
FEATURE [Part::Cylinder] Cylinder079  label="Cylinder131"
  Angle = 360
  Height = 14.5
  Placement = pos=(-43.6,-2.4,-15) rot=(0,0,1;0rad)
  Radius = 0.8
FEATURE [Part::Cylinder] Cylinder080  label="Cylinder132"
  Angle = 360
  Height = 14.5
  Placement = pos=(-43.6,-13.8,-15) rot=(0,0,1;0rad)
  Radius = 0.8
FEATURE [Part::Fuse] Fusion110
  Base = -> Cut045022
  Tool = -> Cut045024
FEATURE [Part::Box] Box043  label="Cube041"
  Height = 4
  Length = 12
  Placement = pos=(-50,-16.75,-14) rot=(0,0,1;0rad)
  Width = 26.75
FEATURE [Part::Chamfer] Chamfer
  Base = -> Box043
  Edges = 1 edges r=7: [Edge3]
FEATURE [Part::Cone] Cone
  Angle = 360
  Height = 1.5
  Placement = pos=(-43.6,-2.4,-10) rot=(0,0,1;0rad)
  Radius1 = 2.75
  Radius2 = 1.25
FEATURE [Part::Cone] Cone001
  Angle = 360
  Height = 1.5
  Placement = pos=(-43.6,-13.8,-10) rot=(0,0,1;0rad)
  Radius1 = 2.75
  Radius2 = 1.25
FEATURE [Part::Fuse] Fusion111
  Base = -> Cone
  Tool = -> Cone001
FEATURE [Part::Fuse] Fusion112
  Base = -> Chamfer
  Tool = -> Fusion111
FEATURE [Part::Fuse] Fusion113
  Base = -> Cylinder079
  Tool = -> Cylinder080
FEATURE [Part::Cut] Cut045027
  Base = -> Fusion112
  Tool = -> Fusion113
FEATURE [Part::Cylinder] Cylinder081  label="Cylinder133"
  Angle = 360
  Height = 14.5
  Placement = pos=(-43.6,-2.4,-15) rot=(0,0,1;0rad)
  Radius = 0.8
FEATURE [Part::Cylinder] Cylinder082  label="Cylinder134"
  Angle = 360
  Height = 14.5
  Placement = pos=(-43.6,-13.8,-15) rot=(0,0,1;0rad)
  Radius = 0.8
FEATURE [Part::Box] Box044  label="Cube042"
  Height = 4
  Length = 12
  Placement = pos=(-50,-16.75,-14) rot=(0,0,1;0rad)
  Width = 26.75
FEATURE [Part::Chamfer] Chamfer001
  Base = -> Box044
  Edges = 1 edges r=7: [Edge3]
FEATURE [Part::Cone] Cone002
  Angle = 360
  Height = 1.5
  Placement = pos=(-43.6,-2.4,-10) rot=(0,0,1;0rad)
  Radius1 = 2.75
  Radius2 = 1.25
FEATURE [Part::Cone] Cone003
  Angle = 360
  Height = 1.5
  Placement = pos=(-43.6,-13.8,-10) rot=(0,0,1;0rad)
  Radius1 = 2.75
  Radius2 = 1.25
FEATURE [Part::Fuse] Fusion114
  Base = -> Cone002
  Tool = -> Cone003
FEATURE [Part::Fuse] Fusion115
  Base = -> Chamfer001
  Tool = -> Fusion114
FEATURE [Part::Fuse] Fusion116
  Base = -> Cylinder081
  Tool = -> Cylinder082
FEATURE [Part::Cut] Cut045028
  Base = -> Fusion115
  Tool = -> Fusion116
FEATURE [Part::Mirroring] Part__Mirroring005  label="Cut045028 (Mirror #6)"
  Base = (0,0,0)
  Normal = (1,0,0)
  Placement = pos=(27,0,0) rot=(0,0,1;0rad)
  Source = -> Cut045028
FEATURE [Part::Cut] Cut045029
  Base = -> Box010
  Tool = -> Fusion071
FEATURE [Part::Cut] Cut045030
  Base = -> Box011
  Tool = -> Fusion073
FEATURE [Part::MultiFuse] Fusion117
  Shapes = -> [Box015,Box016,Box017]
FEATURE [Part::Fuse] Fusion118
  Base = -> Fusion110
  Tool = -> Fusion117
FEATURE [Part::MultiFuse] Fusion119
  Shapes = -> [Fusion118,Cut045030,Cut045029]
FEATURE [Part::MultiFuse] Fusion120
  Shapes = -> [Fusion119,Part__Mirroring005,Cut045027]
FEATURE [Part::Cut] Cut045031
  Base = -> Fusion120
  Tool = -> Fusion057
FEATURE [Part::Cut] Cut045032
  Base = -> Cut045031
  Tool = -> Fusion058
FEATURE [Part::Cut] Cut045033
  Base = -> Cut045032
  Tool = -> Part__Mirroring003
FEATURE [Part::Cut] Cut045034
  Base = -> Cut045033
  Tool = -> Part__Mirroring004
FEATURE [Part::MultiFuse] Fusion121
  Shapes = -> [Cut045034,Box013,Box012]
FEATURE [Part::Chamfer] Chamfer002
  Base = -> Fusion121
  Edges = 1 edges r=25: [Edge244]
FEATURE [Part::Chamfer] Chamfer003
  Base = -> Fusion121
  Edges = 1 edges r=25: [Edge43]
FEATURE [Part::Chamfer] Chamfer004
  Base = -> Chamfer003
  Edges = 1 edges r=25: [Edge225]
FEATURE [Part::Chamfer] Chamfer005
  Base = -> Chamfer004
  Edges = 1 edges r=30: [Edge58]
FEATURE [Part::Chamfer] Chamfer006
  Base = -> Chamfer005
  Edges = 1 edges r=30: [Edge148]
FEATURE [Part::Fillet] Fillet
  Base = -> Chamfer006
  Edges = 1 edges r=2: [Edge233]
FEATURE [Part::Fillet] Fillet001
  Base = -> Fillet
  Edges = 1 edges r=2: [Edge6]
FEATURE [Part::Fillet] Fillet002
  Base = -> Fillet001
  Edges = 1 edges r=2: [Edge2]
FEATURE [Part::Fillet] Fillet003
  Base = -> Fillet002
  Edges = 1 edges r=2: [Edge357]
FEATURE [Part::Fillet] Fillet004
  Base = -> Fillet003
  Edges = 1 edges r=2: [Edge6]
FEATURE [Part::Fillet] Fillet005
  Base = -> Fillet004
  Edges = 1 edges r=2: [Edge2]
FEATURE [Part::Fillet] Fillet006
  Base = -> Fillet005
  Edges = 1 edges r=2: [Edge407]
FEATURE [Part::Fillet] Fillet007
  Base = -> Fillet006
  Edges = 1 edges r=2: [Edge2]
FEATURE [Part::Fillet] Fillet008
  Base = -> Fillet007
  Edges = 1 edges r=2: [Edge369]
FEATURE [Part::Fillet] Fillet009
  Base = -> Fillet008
  Edges = 1 edges r=2: [Edge2]
FEATURE [Part::Cylinder] Cylinder083  label="Cylinder135"
  Angle = 360
  Height = 28
  Placement = pos=(45,6,47) rot=(-0.707107,0,-0.707107;2.26893rad)
  Radius = 0.5
FEATURE [Part::Cylinder] Cylinder084  label="Cylinder136"
  Angle = 360
  Height = 28
  Placement = pos=(66,6,26) rot=(0.707107,0,0.707107;4.01426rad)
  Radius = 0.5
FEATURE [Part::Cut] Cut045035
  Base = -> Fillet009
  Tool = -> Cylinder083
FEATURE [Part::Cut] Cut045036
  Base = -> Cut045035
  Tool = -> Cylinder084
FEATURE [Part::Cylinder] Cylinder085  label="Cylinder137"
  Angle = 360
  Height = 28
  Placement = pos=(66,6,26) rot=(0.707107,0,0.707107;4.01426rad)
  Radius = 0.5
FEATURE [Part::Mirroring] Part__Mirroring006  label="Cylinder137 (Mirror #7)"
  Base = (0,0,0)
  Normal = (1,0,0)
  Placement = pos=(27,0,0) rot=(0,0,1;0rad)
  Source = -> Cylinder085
FEATURE [Part::Cylinder] Cylinder086  label="Cylinder138"
  Angle = 360
  Height = 28
  Placement = pos=(45,6,47) rot=(0.707107,0,0.707107;4.01426rad)
  Radius = 0.5
FEATURE [Part::Mirroring] Part__Mirroring007  label="Cylinder138 (Mirror #8)"
  Base = (0,0,0)
  Normal = (1,0,0)
  Placement = pos=(27,0,0) rot=(0,0,1;0rad)
  Source = -> Cylinder086
FEATURE [Part::Cut] Cut045037
  Base = -> Cut045036
  Tool = -> Part__Mirroring006
FEATURE [Part::Cut] Cut045038
  Base = -> Cut045037
  Tool = -> Part__Mirroring007
